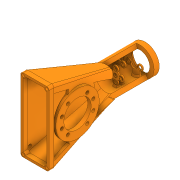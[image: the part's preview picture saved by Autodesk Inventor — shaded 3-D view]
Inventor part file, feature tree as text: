
AUTODESK INVENTOR PART (.ipt)
format: ipt  version: 2020 (Build 240168000, 168)  size: 1,307,648 bytes
history: native  units: in
note: dims shown in document units (in); Inventor stores cm internally (conversion verified against a paired STEP export)
features: sketch x25, chamfer x23, extrude x22, projected_geometry x12, plane x3, loft x2, fillet x1, other x1
ambient origin geometry x8: Origin, YZ Plane, XZ Plane, XY Plane, X Axis, Y Axis, Z Axis, Center Point
bodies: Solid1 (feature_tree)
feature tree (89):
  extrude  "Extrusion1"  Depth=2.0472in
  extrude  "Extrusion2"  Depth=1.6535in
  chamfer  "Chamfer1"  Distance=0.5512in
  extrude  "Extrusion3"  Depth=0.0157in
  extrude  "Extrusion4"  Depth=0.2756in TaperAngle=0.0deg
  extrude  "Extrusion5"  Depth=0.315in
  extrude  "Extrusion6"  Depth=0.4724in
  extrude  "Extrusion7"  Depth=0.0787in
  plane  "Work Plane1"
  extrude  "Extrusion8"  Depth=0.1575in
  plane  "Work Plane2"
  extrude  "Extrusion9"  Depth=1.0994in
  sketch  "Sketch11"  dims[d31=15.0deg d32=0.4921in d33=0.0in]
  plane  "Work Plane3"
  extrude  "Extrusion10"  Depth=0.4921in TaperAngle=0.0deg
  extrude  "Extrusion11"  Depth=1.5748in TaperAngle=360.0deg
  loft  "Loft1"
  loft  "Loft2"
  sketch  "Sketch16"  dims[d47=0.315in d48=0.4331in]
  extrude  "Extrusion12"  Depth=0.0984in TaperAngle=0.0deg
  extrude  "Extrusion13"  Depth=0.4331in
  extrude  "Extrusion14"  Depth=0.6161in
  extrude  "Extrusion15"  Depth=0.1575in
  chamfer  "Chamfer2"  Distance=0.0984in
  chamfer  "Chamfer3"  Distance=0.1969in
  chamfer  "Chamfer4"  Distance=0.1969in
  chamfer  "Chamfer5"  Distance=0.3484in
  chamfer  "Chamfer6"  Distance=0.3484in
  chamfer  "Chamfer7"  Distance=0.1969in
  chamfer  "Chamfer8"  Distance=0.1969in
  chamfer  "Chamfer9"  Distance=0.1969in
  chamfer  "Chamfer10"  Distance=0.3937in
  chamfer  "Chamfer11"  Distance=0.7874in
  chamfer  "Chamfer12"  Angle=90.0deg  [1 undecoded]
  chamfer  "Chamfer13"  Angle=90.0deg  [1 undecoded]
  chamfer  "Chamfer14"  Angle=90.0deg  [1 undecoded]
  chamfer  "Chamfer15"  Angle=90.0deg  [1 undecoded]
  chamfer  "Chamfer16"  Distance=0.7874in
  chamfer  "Chamfer17"  Distance=0.3937in
  chamfer  "Chamfer18"  Distance=0.3937in
  chamfer  "Chamfer19"  Distance=0.7874in
  chamfer  "Chamfer20"  Distance=0.1969in
  chamfer  "Chamfer21"  Distance=0.8858in
  chamfer  "Chamfer22"  Distance=1.6654in
  fillet  "Fillet1"  Radius=1.6654in
  chamfer  "Chamfer23"  [1 undecoded]
  extrude  "Extrusion19"  TaperAngle=0.0deg  [1 undecoded]
  extrude  "Extrusion20"  Depth=0.3937in
  extrude  "Extrusion21"  Depth=0.3937in
  extrude  "Extrusion22"  Depth=0.3937in
  extrude  "Extrusion23"  Depth=0.3937in
  extrude  "Extrusion24"  Depth=0.3937in
  extrude  "Extrusion25"  Depth=0.3937in
  sketch  "Sketch1"  dims[d0=2.3622in d1=2.0472in]
  sketch  "Sketch2"  dims[d2=0.2756in d3=0.0in d4=1.6535in d5=0.5512in d6=0.0in]
  sketch  "Sketch3"  dims[d7=0.2756in d8=0.125in d9=0.0137in d10=0.0157in]
  sketch  "Sketch5"  dims[d11=4.7244in d13=360.0deg d15=0.2756in d16=0.0in]
  sketch  "Sketch6"  dims[d17=0.5512in d19=0.315in]
  projected_geometry  "Projected Loop1"
  sketch  "Sketch7"  dims[d20=0.315in d21=0.4724in]
  projected_geometry  "Projected Loop2"
  sketch  "Sketch8"  dims[d22=0.4724in d23=0.0787in d24=0.0787in d25=0.0787in]
  projected_geometry  "Projected Loop3"
  sketch  "Sketch9"  dims[d26=0.0984in d27=0.0in d28=0.1575in]
  sketch  "Sketch10"  dims[d29=0.1575in d30=1.0994in]
  sketch  "Sketch12"  dims[d34=1.4567in d35=0.0in d36=1.5748in d38=360.0deg]
  sketch  "Sketch13"  dims[d40=0.0787in d41=0.0787in]
  projected_geometry  "Projected Loop4"
  other  "Edges1"
  sketch  "Sketch14"  dims[d42=0.0787in d43=0.0787in]
  projected_geometry  "Projected Loop5"
  sketch  "Sketch15"  dims[d44=0.0787in d45=0.0984in d46=0.0in]
  projected_geometry  "Projected Loop6"
  projected_geometry  "Projected Loop7"
  sketch  "Sketch19"  dims[d49=0.0984in d50=0.0in d51=0.6161in]
  projected_geometry  "Projected Loop8"
  sketch  "Sketch20"  dims[d52=0.1575in d53=0.1575in d54=0.0984in d55=0.0in]
  projected_geometry  "Projected Loop9"
  sketch  "Sketch21"  dims[d56=6.6929in]
  sketch  "Sketch25"  dims[d57=0.8858in]
  sketch  "Sketch26"  dims[d58=1.6654in]
  projected_geometry  "Projected Loop11"
  sketch  "Sketch27"  dims[d59=1.6654in]
  projected_geometry  "Projected Loop12"
  sketch  "Sketch28"  dims[d60=0.0in]
  sketch  "Sketch29"  dims[d61=0.0in]
  sketch  "Sketch30"  dims[d62=1.6654in]
  sketch  "Sketch31"  dims[d63=1.6654in d64=0.1969in d65=0.1969in d66=0.3484in d67=0.3484in d68=0.1969in d69=0.1969in d70=0.1969in d71=0.3937in d72=0.0in d73=0.7874in d74=0.0in d75=0.0in d76=90.0deg d77=0.0in d78=90.0deg d79=0.0in d80=90.0deg d81=0.0in d82=90.0deg d86=0.7874in d87=0.0in d90=0.3937in d91=0.3937in d92=0.7874in d93=0.0in d94=0.1969in d95=0.0in d96=0.8858in d97=1.6654in d98=1.6654in d99=0.0in d100=0.0in d101=0.2224in d102=0.1575in d103=0.1575in d104=0.1575in d105=0.1575in d106=0.0984in d107=0.0984in d108=0.1969in d109=0.0in d122=0.1575in d123=0.0787in d124=45.0deg d125=0.0787in d126=0.1575in d127=45.0deg d128=0.1575in d129=0.0787in d130=45.0deg d131=0.0787in d132=0.1575in d133=45.0deg d134=0.1575in d135=0.0787in d136=45.0deg d137=0.1575in d138=0.0787in d139=45.0deg d140=0.1575in d141=0.0787in d142=45.0deg d143=0.1575in d144=0.0787in d145=45.0deg d146=0.0787in d147=0.1575in d148=45.0deg d149=0.1575in d150=0.0787in d151=45.0deg d152=0.1575in d153=0.0787in d154=45.0deg d155=0.0787in d156=0.1575in d157=45.0deg d158=0.0591in d159=0.1575in d160=0.0137in d161=0.0591in d162=0.1575in d163=0.0137in d164=0.0591in d165=0.1575in d166=0.0137in d167=0.0591in d168=0.1575in d169=0.0137in d170=0.0591in d171=0.1575in d172=0.0137in d173=0.0591in d174=0.1575in d175=0.0137in d176=0.0591in d177=0.1575in d178=0.0137in d179=0.0591in d180=0.1575in d181=0.0137in d182=0.0591in d183=0.1575in d184=0.0137in d185=0.0118in d193=0.0984in d194=0.3937in d195=0.125in d196=45.0deg d197=0.2756in d198=0.1969in d199=0.0in d200=0.2756in d201=2.7559in d202=0.2756in d203=0.2756in d204=0.2756in d205=0.2756in d206=0.2756in d207=0.2756in d208=0.2756in d209=0.0394in d210=0.2047in d211=0.0in d212=0.1969in d213=0.2756in d214=0.0in d215=1.0in d216=0.0in d217=0.2362in d218=0.2362in d219=0.2362in d220=0.2362in d221=0.2362in d222=0.0in d223=0.3937in d224=0.0in d225=0.1575in d226=0.0in d227=0.315in]
  projected_geometry  "Projected Loop13"
note: 6 required parameter values undecoded (feature->parameter linkage not recoverable at this tier; creation-order binding heuristic only, values carry confidence <= 0.55)
